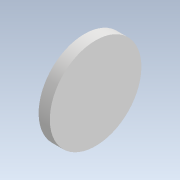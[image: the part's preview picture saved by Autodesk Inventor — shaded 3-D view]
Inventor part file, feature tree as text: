
AUTODESK INVENTOR PART (.ipt)
format: ipt  version: 2021 (Build 250183000, 183)  size: 152,064 bytes
history: native  units: mm
features: sketch x3, other x2, extrude x2, hole x1, chamfer x1, fillet x1, pattern_circular x1
ambient origin geometry x8: Origin, YZ Plane, XZ Plane, XY Plane, X Axis, Y Axis, Z Axis, Center Point
bodies: Body1 (feature_tree)
feature tree (11):
  other  "Sólido1"
  extrude  "Extrusión1"  Depth=8.0mm
  hole  "Agujero1"  [1 undecoded]
  chamfer  "Chaflán1"  Distance=3.0mm
  extrude  "Extrusión2"  TaperAngle=0.0deg  [1 undecoded]
  other  "Eje de trabajo1"
  fillet  "Empalme1"  Radius=0.5mm
  pattern_circular  "Patrón circular1"  Count=4 Angle=360.0deg
  sketch  "Boceto1"  dims[d0=8.0mm d1=0.0mm]
  sketch  "Boceto2"  dims[d2=31.376202mm d3=66.0mm d4=4.0mm d5=2.0mm d6=90.0deg d7=8.0mm d8=20.594885mm d9=50.0mm]
  sketch  "Boceto3"  dims[d10=1.0mm d11=2.0mm d12=45.0deg d13=6.0mm d14=3.0mm d15=0.0mm d16=0.0mm d17=0.5mm d18=40.0mm d19=360.0deg]
note: 2 required parameter values undecoded (feature->parameter linkage not recoverable at this tier; creation-order binding heuristic only, values carry confidence <= 0.55)
